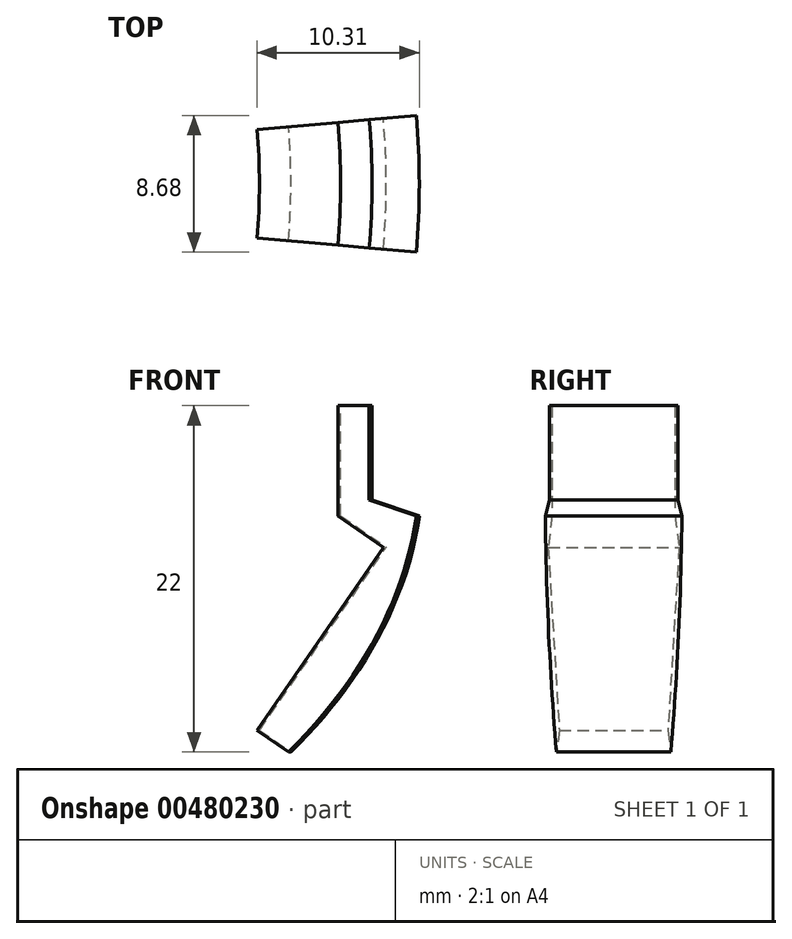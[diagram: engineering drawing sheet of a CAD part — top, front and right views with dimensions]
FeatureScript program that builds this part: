
annotation { "Feature Type Name" : "Feature", "Feature Type Description" : "" }
export const myFeature = defineFeature(function(context is Context, id is Id, definition is map)
    precondition{}
    {
        {
            var Q0;
            Q0=qCreatedBy(makeId("Front.planeOp"),FACE);
            var sketch = newSketch(context, id + "F0", { "sketchPlane" : qUnion([Q0])});
            skEllipse(sketch, "E0", {"center": v(0, 0) * mm, "majorRadius": 50 * mm, "minorRadius": 32.5 * mm, "majorAxis": v(1, 0)});
            skLineSegment(sketch, "E1", {"start": v(49.79, -3) * mm, "end": v(46.79, -2) * mm});
            skLineSegment(sketch, "E2", {"start": v(46.79, -2) * mm, "end": v(46.79, 4) * mm});
            skLineSegment(sketch, "E3", {"start": v(46.79, 4) * mm, "end": v(44.79, 4) * mm});
            skLineSegment(sketch, "E4", {"start": v(44.79, 4) * mm, "end": v(44.79, -3) * mm});
            skLineSegment(sketch, "E5", {"start": v(44.79, -3) * mm, "end": v(47.69, -5) * mm});
            skLineSegment(sketch, "E6", {"start": v(47.69, -5) * mm, "end": v(43.66, -10.8) * mm});
            skLineSegment(sketch, "E7", {"start": v(39.63, -16.61) * mm, "end": v(41.63, -18) * mm});
            skLineSegment(sketch, "E8", {"start": v(0, 32.5) * mm, "end": v(50, 0) * mm, "construction": true});
            skLineSegment(sketch, "E9", {"start": v(0, 58.38) * mm, "end": v(0, -54.04) * mm, "construction": true});
            skPoint(sketch, "E9.endSnap0", {"position": v(0, -32.5) * mm});
            skLineSegment(sketch, "E10", {"start": v(43.66, -10.8) * mm, "end": v(39.63, -16.61) * mm});
            skSolve(sketch);
        }
        {
            var Q0;
            {var subQ0=sQuery(id+"F0.wireOp",EDGE,"E1");Q0=makeQuery(id+"F0.imprint","IMPRINT",FACE,{"disambiguationData":[TD([[makeQuery(id+"F0.imprint","IMPRINT",EDGE,{"derivedFrom":subQ0}),1.0]])]});}
            var Q1;
            Q1=sQuery(id+"F0.wireOp",EDGE,"E9");
            revolve(context, id + "F1", {"entities" : qUnion([Q0]), "axis" : qUnion([Q1]), "revolveType" : RevolveType.SYMMETRIC, "angle" : 10 * degree});
        }
    });
